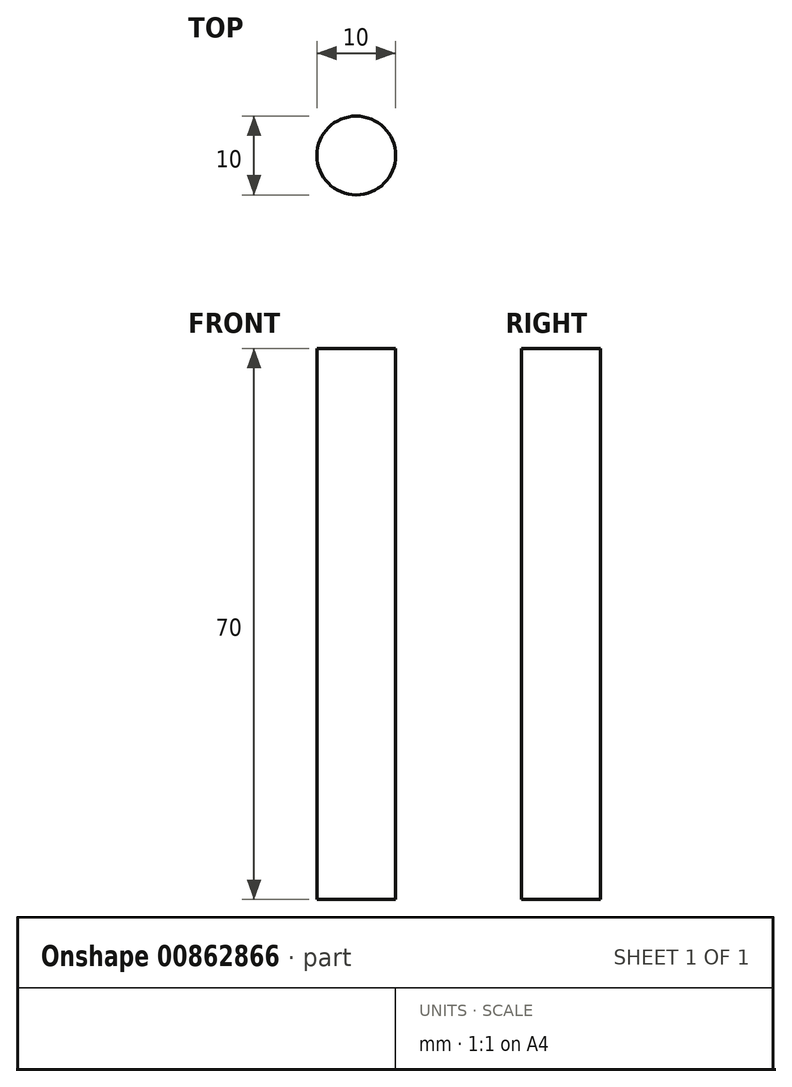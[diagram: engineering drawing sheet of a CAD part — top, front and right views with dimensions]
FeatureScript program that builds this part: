
annotation { "Feature Type Name" : "Feature", "Feature Type Description" : "" }
export const myFeature = defineFeature(function(context is Context, id is Id, definition is map)
    precondition{}
    {
        {
            var Q0;
            Q0=qCreatedBy(makeId("Top.planeOp"),FACE);
            var sketch = newSketch(context, id + "F0", { "sketchPlane" : qUnion([Q0])});
            skCircle(sketch, "E0", {"center": v(0, 0) * mm, "radius": 5 * mm});
            skSolve(sketch);
        }
        {
            var Q0;
            Q0 = qSketchRegion(id + "F0", true);
            extrude(context, id + "F1", {"entities" : qUnion([Q0]), "depth" : 70 * mm, "offsetDistance" : 25.4 * mm});
        }
    });
